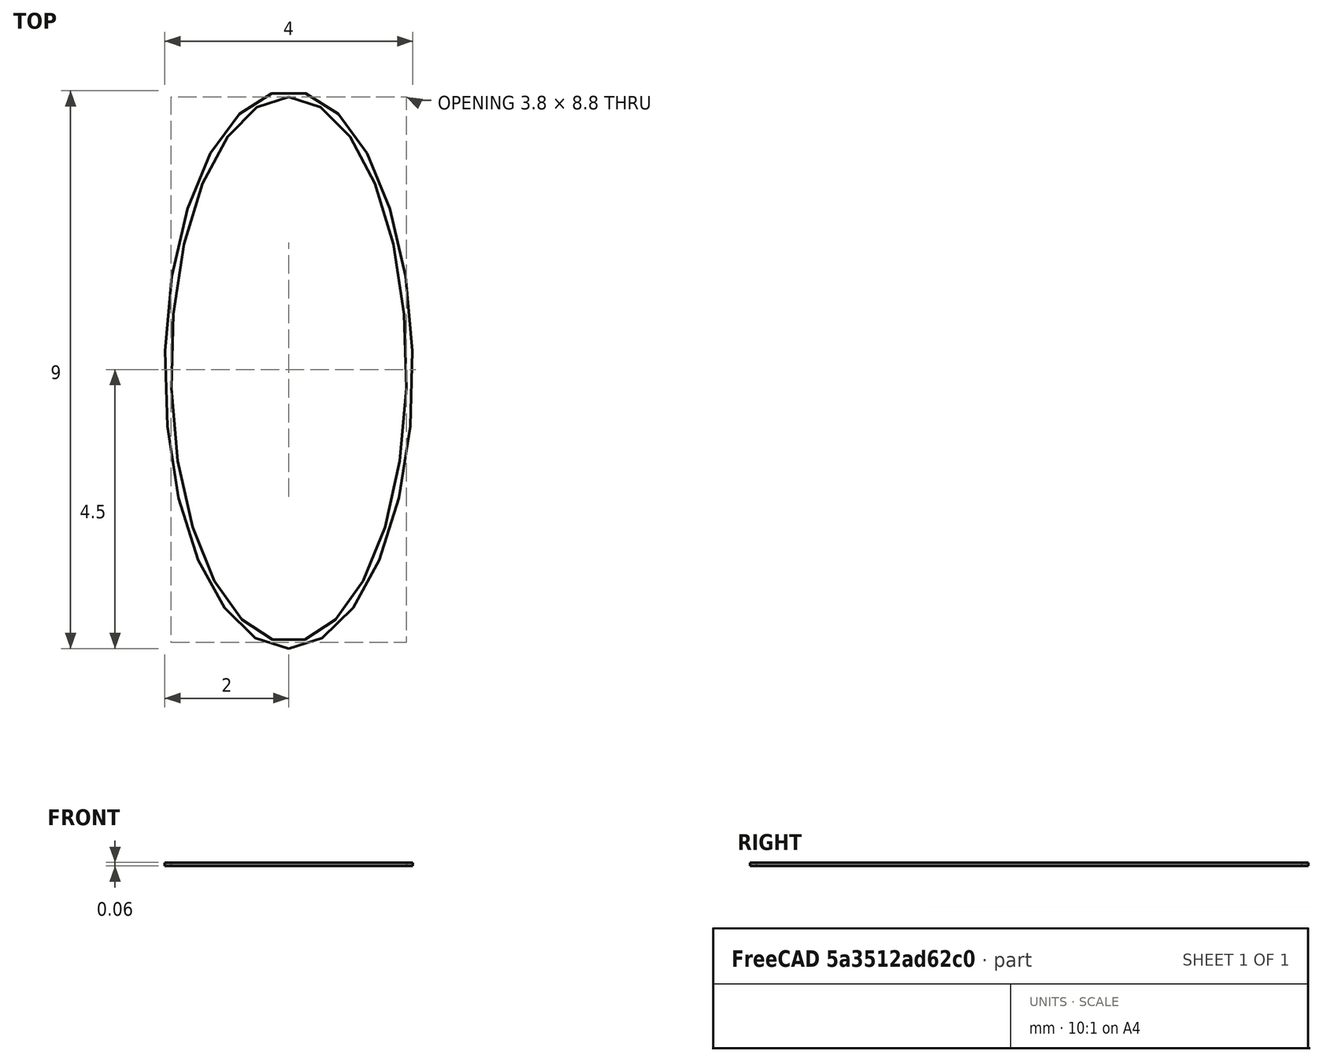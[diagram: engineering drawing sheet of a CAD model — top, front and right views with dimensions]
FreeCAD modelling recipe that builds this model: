
FCSTD DOCUMENT  (FreeCAD 0.16R6712 (Git))
Label: 0t
License: All rights reserved
LicenseURL: http://en.wikipedia.org/wiki/All_rights_reserved
objects: Sketcher::SketchObject×1, PartDesign::Pad×1, Mesh::Feature×1
note: 3 computed .brp shape members not serialized (recipe doc carries the construction recipe); baked Part::Feature solids carry a one-line shape summary decoded from their .brp

FEATURE [Sketcher::SketchObject] Sketch
  sketch-geometry (10):
    g0: Ellipse CenterX=0 CenterY=4.5 CenterZ=0 NormalX=0 NormalY=0 NormalZ=1 MajorRadius=4.5 MinorRadius=2 AngleXU=-1.5708
    g1: LineSegment [constr] StartX=0 StartY=0 StartZ=0 EndX=0 EndY=9 EndZ=0
    g2: LineSegment [constr] StartX=2 StartY=4.5 StartZ=0 EndX=-2 EndY=4.5 EndZ=0
    g3: GeomPoint [constr] X=0 Y=0.468871 Z=0
    g4: GeomPoint [constr] X=0 Y=8.53113 Z=0
    g5: Ellipse CenterX=0 CenterY=4.5 CenterZ=0 NormalX=0 NormalY=0 NormalZ=1 MajorRadius=4.4 MinorRadius=1.9 AngleXU=1.5708
    g6: LineSegment [constr] StartX=0 StartY=8.9 StartZ=0 EndX=0 EndY=0.1 EndZ=0
    g7: LineSegment [constr] StartX=-1.9 StartY=4.5 StartZ=0 EndX=1.9 EndY=4.5 EndZ=0
    g8: GeomPoint [constr] X=0 Y=8.46863 Z=0
    g9: GeomPoint [constr] X=0 Y=0.531373 Z=0
  constraints (11):
    c: InternalAlignment(g1-g4 -> g0) x4
    c: PointOnObject(g0,g-2)
    c: PointOnObject(g-1,g0)
    c: Distance(g2,g0) = 2
    c: PointOnObject(g1,g-2)
    c: InternalAlignment(g6-g9 -> g5) x4
    c: Coincident(g5,g0)
    c: DistanceY(g-1,g0) = 4.5
    c: DistanceY(g6,g1) = 0.1
    c: DistanceX(g7,g2) = 0.1
    c: PointOnObject(g6,g-2)
FEATURE [PartDesign::Pad] Pad
  Length = 0.05
  Length2 = 100
  Midplane = true
  Sketch = -> Sketch
  Type = 0
FEATURE [Mesh::Feature] Mesh  label="Pad (Meshed)"
